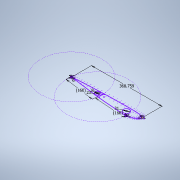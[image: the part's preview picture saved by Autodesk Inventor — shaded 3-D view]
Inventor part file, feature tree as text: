
AUTODESK INVENTOR PART (.ipt)
format: ipt  version: 2022 (Build 260153000, 153)  size: 144,896 bytes
history: native  units: mm
features: sketch x1
ambient origin geometry x8: Origin, YZ Plane, XZ Plane, XY Plane, X Axis, Y Axis, Z Axis, Center Point
feature tree (1):
  sketch  "Sketch1"  dims[d5=160.0mm d8=160.0mm d17=5.0mm d18=5.0mm d25=6.0mm d26=5.0mm d27=5.0mm d31=34.456mm d36=5.0mm d37=5.0mm d41=23.0mm d50=368.759386mm d60=8.0mm d62=31.0mm]
